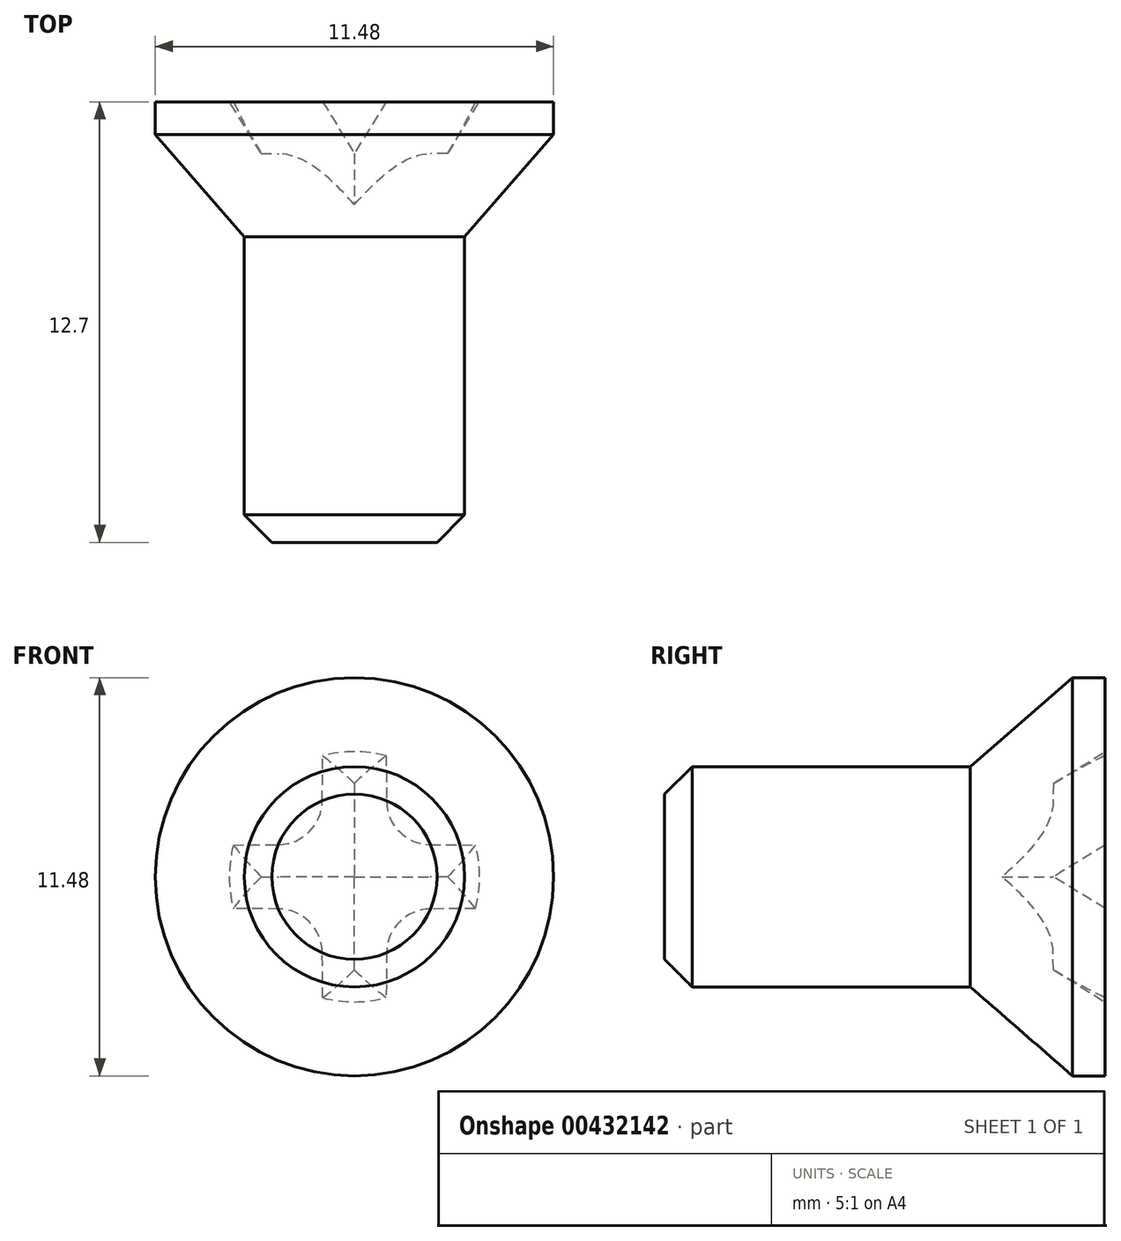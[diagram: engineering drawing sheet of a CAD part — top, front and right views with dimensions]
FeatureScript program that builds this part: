
annotation { "Feature Type Name" : "Feature", "Feature Type Description" : "" }
export const myFeature = defineFeature(function(context is Context, id is Id, definition is map)
    precondition{}
    {
        {
            var Q0;
            Q0=qCreatedBy(makeId("Top.planeOp"),FACE);
            var sketch = newSketch(context, id + "F0", { "sketchPlane" : qUnion([Q0])});
            skLineSegment(sketch, "E0", {"start": v(0, 0) * mm, "end": v(0, -12.7) * mm});
            skLineSegment(sketch, "E1", {"start": v(0, -12.7) * mm, "end": v(3.17, -12.7) * mm});
            skLineSegment(sketch, "E2", {"start": v(3.17, -12.7) * mm, "end": v(3.17, -3.89) * mm});
            skLineSegment(sketch, "E3", {"start": v(3.18, -3.89) * mm, "end": v(5.74, -0.94) * mm});
            skLineSegment(sketch, "E4", {"start": v(5.74, -0.94) * mm, "end": v(5.74, 0) * mm});
            skLineSegment(sketch, "E5", {"start": v(5.74, 0) * mm, "end": v(0, 0) * mm});
            skLineSegment(sketch, "E6", {"start": v(0, -17.59) * mm, "end": v(0, 2.74) * mm, "construction": true});
            skSolve(sketch);
        }
        {
            var Q0;
            Q0=makeQuery(id+"F0.imprint","IMPRINT",FACE,{"disambiguationData":[TD([[makeQuery(id+"F0.imprint","IMPRINT",EDGE,{"derivedFrom":sQuery(id+"F0.wireOp",EDGE,"E0")}),1.0]])]});
            var Q1;
            Q1=sQuery(id+"F0.wireOp",EDGE,"E6");
            revolve(context, id + "F1", {"entities" : qUnion([Q0]), "axis" : qUnion([Q1]), "revolveType" : RevolveType.FULL});
        }
        {
            var Q0;
            Q0=makeQuery(id+"F1.opRevolve","SWEPT_EDGE",EDGE,{"disambiguationData":[OSD([sQuery(id+"F0.wireOp",EDGE,"E1"),sQuery(id+"F0.wireOp",EDGE,"E2")])]});
            chamfer(context, id + "F2", {"entities" : qUnion([Q0]), "width" : 0.8 * mm, "tangentPropagation" : true});
        }
        {
            var Q0;
            Q0=makeQuery(id+"F1.opRevolve","SWEPT_FACE",FACE,{"disambiguationData":[OSD([sQuery(id+"F0.wireOp",EDGE,"E5")])]});
            var sketch = newSketch(context, id + "F3", { "sketchPlane" : qUnion([Q0])});
            skArc(sketch, "E7", {"start": v(-0.91, -3.49) * mm, "mid": v(0, -3.6) * mm, "end": v(0.91, -3.49) * mm});
            skLineSegment(sketch, "E8", {"start": v(0.91, -3.49) * mm, "end": v(0.93, -2.18) * mm});
            skLineSegment(sketch, "E9", {"start": v(-0.91, -3.49) * mm, "end": v(-0.93, -2.18) * mm});
            skLineSegment(sketch, "E10.1.0", {"start": v(3.49, -0.91) * mm, "end": v(2.18, -0.93) * mm});
            skArc(sketch, "E10.1.1", {"start": v(3.49, -0.91) * mm, "mid": v(3.6, 0) * mm, "end": v(3.49, 0.91) * mm});
            skLineSegment(sketch, "E10.1.2", {"start": v(3.49, 0.91) * mm, "end": v(2.18, 0.93) * mm});
            skLineSegment(sketch, "E10.2.0", {"start": v(0.91, 3.49) * mm, "end": v(0.93, 2.18) * mm});
            skArc(sketch, "E10.2.1", {"start": v(0.91, 3.49) * mm, "mid": v(0, 3.6) * mm, "end": v(-0.91, 3.49) * mm});
            skLineSegment(sketch, "E10.2.2", {"start": v(-0.91, 3.49) * mm, "end": v(-0.93, 2.18) * mm});
            skLineSegment(sketch, "E10.3.0", {"start": v(-3.49, 0.91) * mm, "end": v(-2.18, 0.93) * mm});
            skArc(sketch, "E10.3.1", {"start": v(-3.49, 0.91) * mm, "mid": v(-3.6, 0) * mm, "end": v(-3.49, -0.91) * mm});
            skLineSegment(sketch, "E10.3.2", {"start": v(-3.49, -0.91) * mm, "end": v(-2.18, -0.93) * mm});
            skPoint(sketch, "E11.newPointA", {"position": v(-0.92, 0.94) * mm});
            skPoint(sketch, "E11.newPointB", {"position": v(-0.94, 0.94) * mm});
            skArc(sketch, "E11.filletArc", {"start": v(-2.18, 0.93) * mm, "mid": v(-1.3, 1.3) * mm, "end": v(-0.93, 2.18) * mm});
            skPoint(sketch, "E12.newPointA", {"position": v(0.94, 0.92) * mm});
            skPoint(sketch, "E12.newPointB", {"position": v(0.94, 0.94) * mm});
            skArc(sketch, "E12.filletArc", {"start": v(0.93, 2.18) * mm, "mid": v(1.3, 1.3) * mm, "end": v(2.18, 0.93) * mm});
            skPoint(sketch, "E13.newPointA", {"position": v(0.92, -0.94) * mm});
            skPoint(sketch, "E13.newPointB", {"position": v(0.94, -0.94) * mm});
            skArc(sketch, "E13.filletArc", {"start": v(2.18, -0.93) * mm, "mid": v(1.3, -1.3) * mm, "end": v(0.93, -2.18) * mm});
            skPoint(sketch, "E14.newPointA", {"position": v(-0.94, -0.94) * mm});
            skPoint(sketch, "E14.newPointB", {"position": v(-0.94, -0.92) * mm});
            skArc(sketch, "E14.filletArc", {"start": v(-0.93, -2.18) * mm, "mid": v(-1.3, -1.3) * mm, "end": v(-2.18, -0.93) * mm});
            skSolve(sketch);
        }
        {
            var Q0;
            Q0=makeQuery(id+"F3.imprint","IMPRINT",FACE,{"disambiguationData":[TD([[makeQuery(id+"F3.imprint","IMPRINT",EDGE,{"derivedFrom":sQuery(id+"F3.wireOp",EDGE,"E7")}),1.0]])]});
            extrude(context, id + "F4", {"entities" : qUnion([Q0]), "operationType" : NewBodyOperationType.REMOVE, "oppositeDirection" : true, "depth" : 4.34 * mm, "hasDraft" : true, "draftAngle" : 63.5 / 2 * degree, "draftPullDirection" : true});
        }
    });
